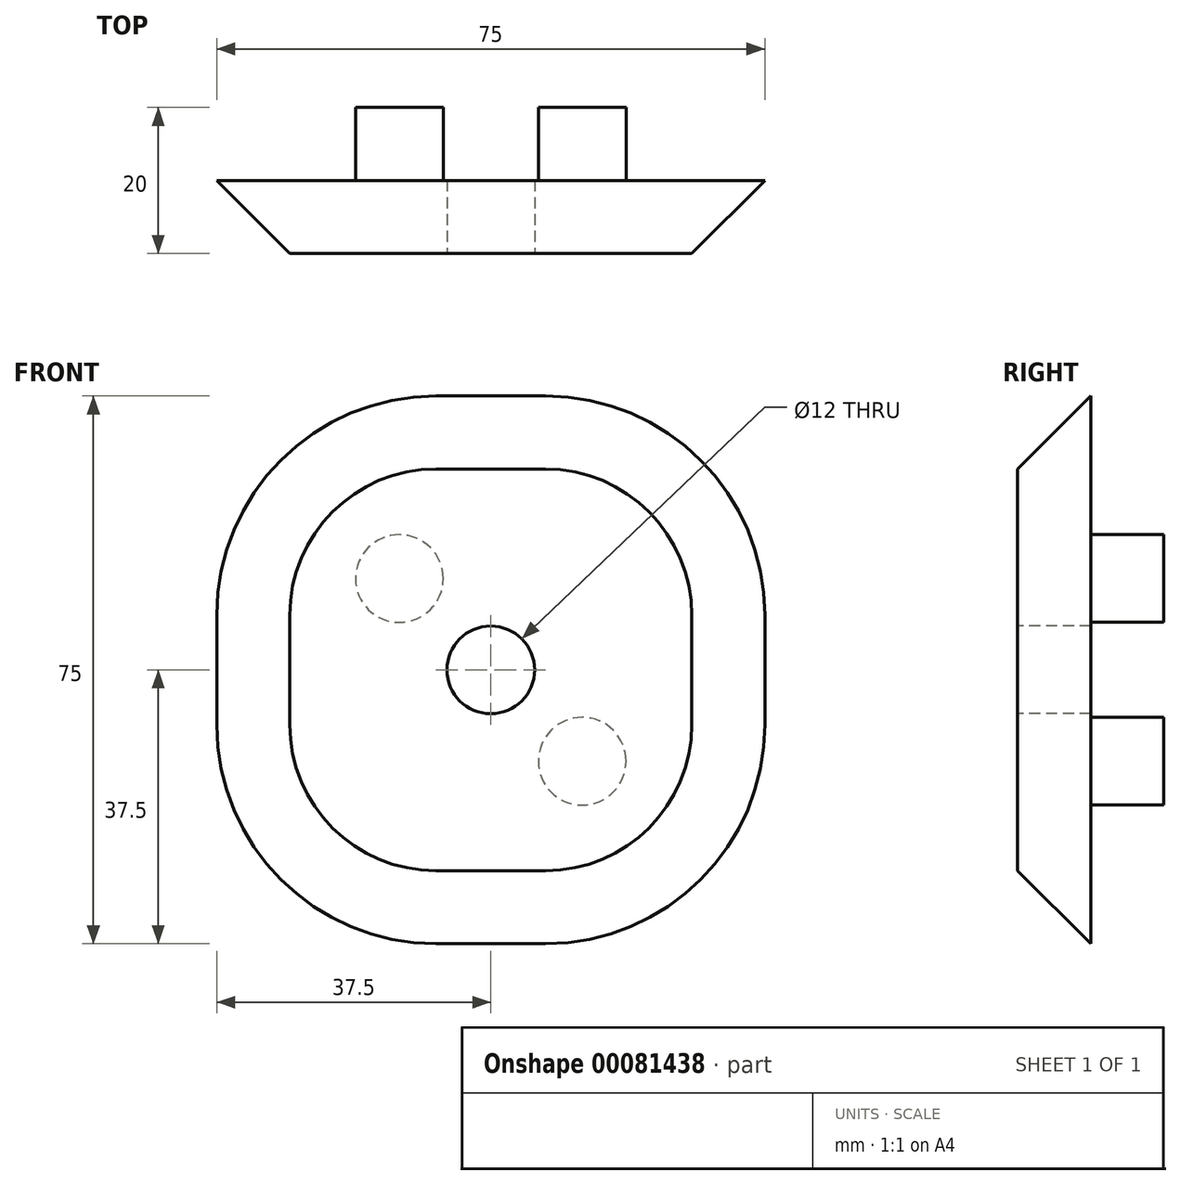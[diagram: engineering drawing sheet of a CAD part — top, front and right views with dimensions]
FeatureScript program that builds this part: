
annotation { "Feature Type Name" : "Feature", "Feature Type Description" : "" }
export const myFeature = defineFeature(function(context is Context, id is Id, definition is map)
    precondition{}
    {
        {
            var Q0;
            Q0=qCreatedBy(makeId("Front.planeOp"),FACE);
            var sketch = newSketch(context, id + "F0", { "sketchPlane" : qUnion([Q0])});
            skLineSegment(sketch, "E0.bottom", {"start": v(0, 0) * mm, "end": v(-75, 0) * mm});
            skLineSegment(sketch, "E0.top", {"start": v(0, 75) * mm, "end": v(-75, 75) * mm});
            skLineSegment(sketch, "E0.left", {"start": v(0, 0) * mm, "end": v(0, 75) * mm});
            skLineSegment(sketch, "E0.right", {"start": v(-75, 0) * mm, "end": v(-75, 75) * mm});
            skSolve(sketch);
        }
        {
            var Q0;
            Q0=makeQuery(id+"F0.imprint","IMPRINT",FACE,{"disambiguationData":[TD([[makeQuery(id+"F0.imprint","IMPRINT",EDGE,{"derivedFrom":sQuery(id+"F0.wireOp",EDGE,"E0.bottom")}),-1.0]])]});
            extrude(context, id + "F1", {"entities" : qUnion([Q0]), "depth" : 20 * mm});
        }
        {
            var Q0;
            Q0=makeQuery(id+"F1.opExtrude","SWEPT_EDGE",EDGE,{"disambiguationData":[OSD([sQuery(id+"F0.wireOp",EDGE,"E0.bottom"),sQuery(id+"F0.wireOp",EDGE,"E0.right")])]});
            var Q1;
            Q1=makeQuery(id+"F1.opExtrude","SWEPT_EDGE",EDGE,{"disambiguationData":[OSD([sQuery(id+"F0.wireOp",EDGE,"E0.bottom"),sQuery(id+"F0.wireOp",EDGE,"E0.left")])]});
            var Q2;
            Q2=makeQuery(id+"F1.opExtrude","SWEPT_EDGE",EDGE,{"disambiguationData":[OSD([sQuery(id+"F0.wireOp",EDGE,"E0.top"),sQuery(id+"F0.wireOp",EDGE,"E0.left")])]});
            var Q3;
            Q3=makeQuery(id+"F1.opExtrude","SWEPT_EDGE",EDGE,{"disambiguationData":[OSD([sQuery(id+"F0.wireOp",EDGE,"E0.top"),sQuery(id+"F0.wireOp",EDGE,"E0.right")])]});
            fillet(context, id + "F2", {"entities" : qUnion([Q0, Q1, Q2, Q3]), "radius" : 30 * mm, "tangentPropagation" : true, "allowEdgeOverflow" : false});
        }
        {
            var Q0;
            Q0=makeQuery(id+"F1.opExtrude","CAP_FACE",FACE,{"disambiguationData":[OSD([sQuery(id+"F0.wireOp",EDGE,"E0.bottom"),sQuery(id+"F0.wireOp",EDGE,"E0.top"),sQuery(id+"F0.wireOp",EDGE,"E0.left"),sQuery(id+"F0.wireOp",EDGE,"E0.right")])],"isStart":false});
            var sketch = newSketch(context, id + "F3", { "sketchPlane" : qUnion([Q0])});
            skLineSegment(sketch, "E1.0", {"start": v(-75, 30) * mm, "end": v(-75, 45) * mm});
            skLineSegment(sketch, "E1.1", {"start": v(-30, 75) * mm, "end": v(-45, 75) * mm});
            skLineSegment(sketch, "E1.2", {"start": v(-30, 0) * mm, "end": v(-45, 0) * mm});
            skLineSegment(sketch, "E1.3", {"start": v(0, 30) * mm, "end": v(0, 45) * mm});
            skArc(sketch, "E1.4", {"start": v(0, 45) * mm, "mid": v(-8.79, 66.21) * mm, "end": v(-30, 75) * mm});
            skArc(sketch, "E1.5", {"start": v(-45, 75) * mm, "mid": v(-66.21, 66.21) * mm, "end": v(-75, 45) * mm});
            skArc(sketch, "E1.6", {"start": v(-75, 30) * mm, "mid": v(-66.21, 8.79) * mm, "end": v(-45, 0) * mm});
            skArc(sketch, "E1.7", {"start": v(-30, 0) * mm, "mid": v(-8.79, 8.79) * mm, "end": v(0, 30) * mm});
            skLineSegment(sketch, "E1.8", {"start": v(-30, 75) * mm, "end": v(-45, 75) * mm});
            skLineSegment(sketch, "E2", {"start": v(-75, 37.5) * mm, "end": v(0, 37.5) * mm, "construction": true});
            skLineSegment(sketch, "E3", {"start": v(0, 37.5) * mm, "end": v(-37.5, 75) * mm, "construction": true});
            skLineSegment(sketch, "E4", {"start": v(-37.5, 75) * mm, "end": v(-37.5, 0) * mm, "construction": true});
            skCircle(sketch, "E5", {"center": v(-37.5, 37.5) * mm, "radius": 6 * mm});
            skSolve(sketch);
        }
        {
            var Q0;
            Q0=makeQuery(id+"F1.opExtrude","CAP_FACE",FACE,{"disambiguationData":[OSD([sQuery(id+"F0.wireOp",EDGE,"E0.bottom"),sQuery(id+"F0.wireOp",EDGE,"E0.top"),sQuery(id+"F0.wireOp",EDGE,"E0.left"),sQuery(id+"F0.wireOp",EDGE,"E0.right")])],"isStart":true});
            var sketch = newSketch(context, id + "F4", { "sketchPlane" : qUnion([Q0])});
            skLineSegment(sketch, "E6.0", {"start": v(75, 37.5) * mm, "end": v(0, 37.5) * mm, "construction": true});
            skLineSegment(sketch, "E6.1", {"start": v(0, 37.5) * mm, "end": v(37.5, 75) * mm, "construction": true});
            skLineSegment(sketch, "E6.2", {"start": v(37.5, 75) * mm, "end": v(37.5, 0) * mm, "construction": true});
            skLineSegment(sketch, "E6.3", {"start": v(0, 30) * mm, "end": v(0, 45) * mm});
            skLineSegment(sketch, "E6.4", {"start": v(75, 30) * mm, "end": v(75, 45) * mm});
            skLineSegment(sketch, "E6.5", {"start": v(30, 0) * mm, "end": v(45, 0) * mm});
            skLineSegment(sketch, "E6.6", {"start": v(30, 75) * mm, "end": v(45, 75) * mm});
            skCircle(sketch, "E7", {"center": v(50, 25) * mm, "radius": 6 * mm});
            skCircle(sketch, "E8.MirrorC", {"center": v(25, 25) * mm, "radius": 6 * mm});
            skCircle(sketch, "E9.MirrorC", {"center": v(25, 50) * mm, "radius": 6 * mm});
            skCircle(sketch, "E10.MirrorC", {"center": v(50, 50) * mm, "radius": 6 * mm});
            skSolve(sketch);
        }
        {
            var Q0;
            Q0=makeQuery(id+"F1.opExtrude","CAP_EDGE",EDGE,{"disambiguationData":[OSD([sQuery(id+"F0.wireOp",EDGE,"E0.right")])],"isStart":false});
            chamfer(context, id + "F5", {"entities" : qUnion([Q0]), "width" : 10 * mm, "tangentPropagation" : true});
        }
        {
            var Q0;
            Q0=makeQuery(id+"F3.imprint","IMPRINT",FACE,{"disambiguationData":[TD([[makeQuery(id+"F3.imprint","IMPRINT",EDGE,{"derivedFrom":sQuery(id+"F3.wireOp",EDGE,"E5")}),-1.0]])]});
            var Q1;
            Q1=makeQuery(id+"F3.imprint","IMPRINT",FACE,{"disambiguationData":[TD([[makeQuery(id+"F3.imprint","IMPRINT",EDGE,{"derivedFrom":sQuery(id+"F3.wireOp",EDGE,"E5")}),1.0]])]});
            var Q2;
            Q2=makeQuery(id+"F3.imprint","IMPRINT",FACE,{"disambiguationData":[TD([[makeQuery(id+"F3.imprint","IMPRINT",EDGE,{"derivedFrom":sQuery(id+"F3.wireOp",EDGE,"E5")}),-1.0]])]});
            var Q3;
            Q3=makeQuery(id+"F3.imprint","IMPRINT",FACE,{"disambiguationData":[TD([[makeQuery(id+"F3.imprint","IMPRINT",EDGE,{"derivedFrom":sQuery(id+"F3.wireOp",EDGE,"E5")}),1.0]])]});
            var Q4;
            Q4=makeQuery(id+"F4.imprint","IMPRINT",FACE,{"disambiguationData":[TD([[makeQuery(id+"F4.imprint","IMPRINT",EDGE,{"derivedFrom":sQuery(id+"F4.wireOp",EDGE,"E9.MirrorC")}),1.0]])]});
            var Q5;
            Q5=makeQuery(id+"F4.imprint","IMPRINT",FACE,{"disambiguationData":[TD([[makeQuery(id+"F4.imprint","IMPRINT",EDGE,{"derivedFrom":sQuery(id+"F4.wireOp",EDGE,"E10.MirrorC")}),-1.0]])]});
            var Q6;
            Q6=makeQuery(id+"F4.imprint","IMPRINT",FACE,{"disambiguationData":[TD([[makeQuery(id+"F4.imprint","IMPRINT",EDGE,{"derivedFrom":sQuery(id+"F4.wireOp",EDGE,"E7")}),1.0]])]});
            var Q7;
            Q7=makeQuery(id+"F4.imprint","IMPRINT",FACE,{"disambiguationData":[TD([[makeQuery(id+"F4.imprint","IMPRINT",EDGE,{"derivedFrom":sQuery(id+"F4.wireOp",EDGE,"E8.MirrorC")}),-1.0]])]});
            extrude(context, id + "F6", {"entities" : qUnion([Q0, Q1, Q2, Q3, Q4, Q5, Q6, Q7]), "operationType" : NewBodyOperationType.REMOVE, "oppositeDirection" : true, "depth" : 10 * mm});
        }
        {
            var Q0;
            Q0=makeQuery(id+"F4.imprint","IMPRINT",FACE,{"disambiguationData":[TD([[makeQuery(id+"F4.imprint","IMPRINT",EDGE,{"derivedFrom":sQuery(id+"F4.wireOp",EDGE,"E9.MirrorC")}),1.0]])]});
            var Q1;
            Q1=makeQuery(id+"F4.imprint","IMPRINT",FACE,{"disambiguationData":[TD([[makeQuery(id+"F4.imprint","IMPRINT",EDGE,{"derivedFrom":sQuery(id+"F4.wireOp",EDGE,"E10.MirrorC")}),-1.0]])]});
            var Q2;
            Q2=makeQuery(id+"F4.imprint","IMPRINT",FACE,{"disambiguationData":[TD([[makeQuery(id+"F4.imprint","IMPRINT",EDGE,{"derivedFrom":sQuery(id+"F4.wireOp",EDGE,"E7")}),1.0]])]});
            var Q3;
            Q3=makeQuery(id+"F4.imprint","IMPRINT",FACE,{"disambiguationData":[TD([[makeQuery(id+"F4.imprint","IMPRINT",EDGE,{"derivedFrom":sQuery(id+"F4.wireOp",EDGE,"E8.MirrorC")}),-1.0]])]});
            extrude(context, id + "F7", {"entities" : qUnion([Q0, Q1, Q2, Q3]), "operationType" : NewBodyOperationType.REMOVE, "oppositeDirection" : true, "depth" : 10 * mm});
        }
    });
